# Revit family: Backflow_Preventer-DCDA-Zurn_Wilkins-Model_450DABG-(4-6_Inch)
name_source: partatom
category: Pipe Accessories
units: mm (PartAtom-declared; Revit-internal decimal feet)

## family parameters
Always vertical = Yes
Cut with Voids When Loaded = No
OmniClass Number = 23.65.55.14.21
OmniClass Title = Non-Return Valves for Liquid Services
Part Type = Valve - Breaks Into
Round Connector Dimension = Use Radius
Shared = No
Work Plane-Based = No

## types (2) — shared parameters
Assembly Code = D2020300
Bend Radius = 1 1/4"
Bend Radius Outside = 2 3/8"
Default Elevation = 0"
Description = Double Check Detector Assembly
Flow Rate (GPM) = 0 GPM
Hydrostatic Test Pressure = 350.00 psi
Main Material = Paint - Zurn - Blue - Ductile Iron
Manufacturer = Zurn Water, LLC
Manufacturer Brand = Zurn Wilkins
Max Working Water Pressure = 175.00 psi
Max Working Water Temperature = 140 °F
Model = 450DABG
Modified Date = 07/16/2025
Pipe Size = 1"
Product Documentation Link = https://files.zurn.com
Product Installation Sheet URL = https://files.zurn.com
Product Page URL = https://www.zurn.com
Product data URL = https://www.bimobject.com
Repair Parts URL = https://files.zurn.com
URL = https://www.zurn.com

## per-type parameters (varying)
| type | DIM A - Inlet center to outlet center | DIM B - Total height of the valve | DIM C - Center to gate valve stem top | DIM D - Center to bypass end | Gate valve | Height | Length | Main Body | Nominal Diameter | Nominal Radius | Overall Height | Overall Length | Pipe Position | Pipe Vertical Position | Pressure Loss at Rated Flow | Product Weight (lbs) | Rated Flow |
| 6-450DABG (6" 450DABG) | 18 11/16" | 32 1/8" | 10 1/4" | 10" | Shut_Off_Valve-Butterfly-Zurn_Wilkins-Model_49G_Grooved-(2.5-10)_Inch : 6-49G (6" 49G) | 35 1/2" | 18 11/16" | Main Body 450DA 4&6 : 6" | 6" | 3" | 35 1/2" | 18 11/16" | 8 3/4" | 6 1/4" | 5.00 psi | 248 | 1000 GPM |
| 4-450DABG (4" 450DABG) | 18 5/16" | 27 3/4" | 9" | 8" | Shut_Off_Valve-Butterfly-Zurn_Wilkins-Model_49G_Grooved-(2.5-10)_Inch : 4-49G (4" 49G) | 30" | 18 5/16" | Main Body 450DA 4&6 : 4" | 4" | 2" | 30" | 18 5/16" | 6 3/8" | 7 1/4" | 5.80 psi | 153 | 500 GPM |

## geometry (parser evidence)
native form markers: Sweep x14
no freeform markers — native parametric forms only
